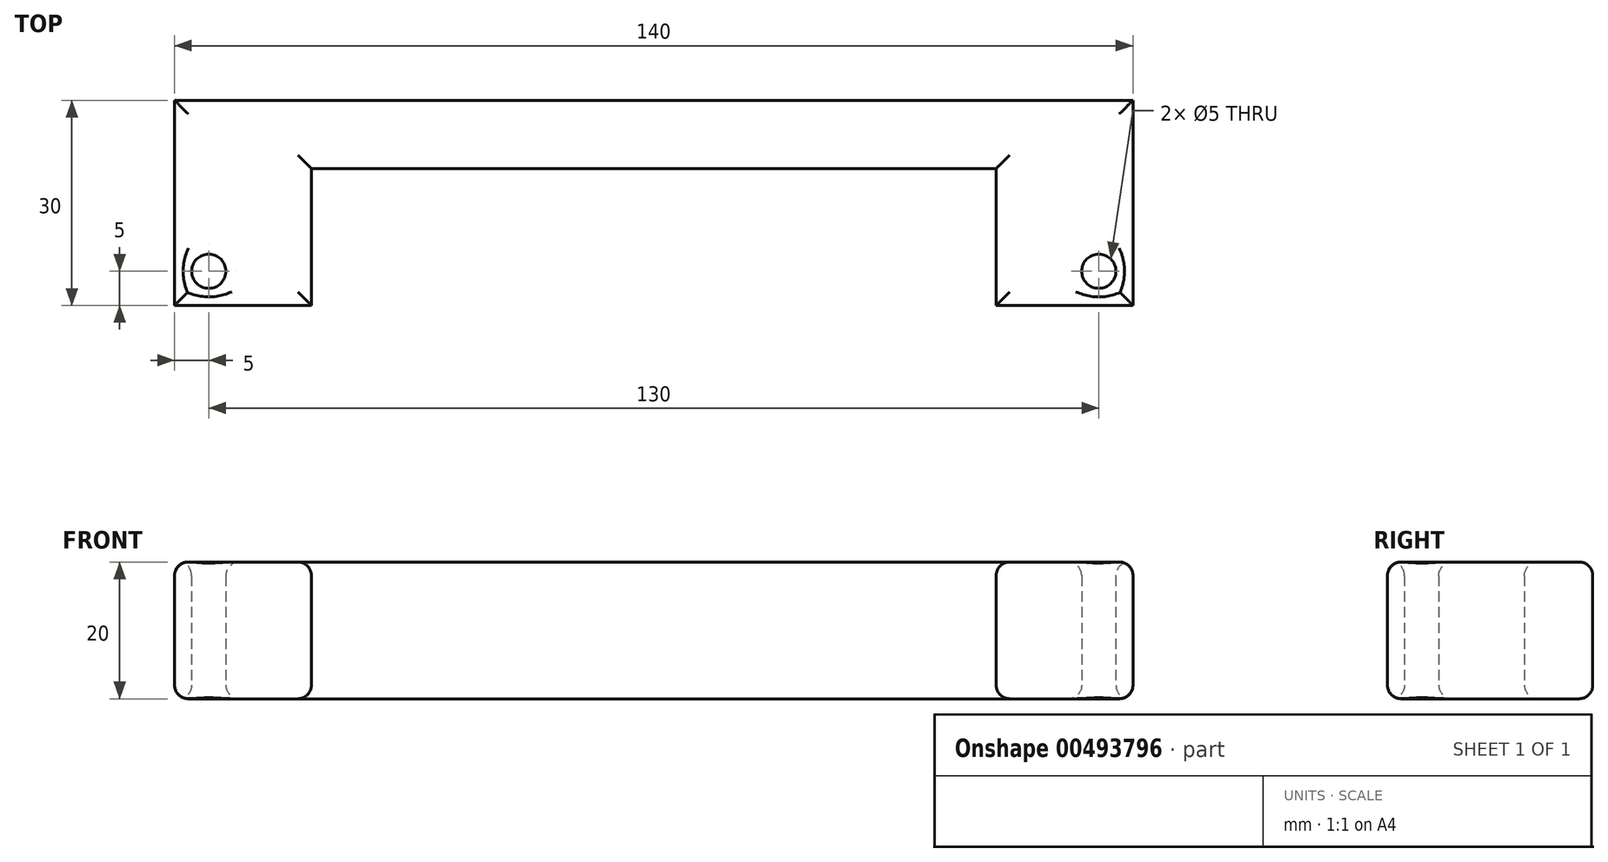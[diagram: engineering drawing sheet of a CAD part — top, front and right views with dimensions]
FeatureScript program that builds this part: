
annotation { "Feature Type Name" : "Feature", "Feature Type Description" : "" }
export const myFeature = defineFeature(function(context is Context, id is Id, definition is map)
    precondition{}
    {
        {
            var Q0;
            Q0=qCreatedBy(makeId("Top.planeOp"),FACE);
            var sketch = newSketch(context, id + "F0", { "sketchPlane" : qUnion([Q0])});
            skLineSegment(sketch, "E0", {"start": v(0, 30) * mm, "end": v(0, 20) * mm});
            skLineSegment(sketch, "E1", {"start": v(0, 20) * mm, "end": v(50, 20) * mm});
            skLineSegment(sketch, "E2", {"start": v(50, 20) * mm, "end": v(50, 0) * mm});
            skLineSegment(sketch, "E3", {"start": v(50, 0) * mm, "end": v(70, 0) * mm});
            skLineSegment(sketch, "E4", {"start": v(70, 0) * mm, "end": v(70, 30) * mm});
            skLineSegment(sketch, "E5", {"start": v(0, 30) * mm, "end": v(70, 30) * mm});
            skLineSegment(sketch, "E6", {"start": v(70, 30) * mm, "end": v(70, 30) * mm});
            skSolve(sketch);
        }
        {
            var Q0;
            Q0 = qSketchRegion(id + "F0", true);
            extrude(context, id + "F1", {"entities" : qUnion([Q0]), "depth" : 20 * mm});
        }
        {
            var Q0;
            Q0=qCreatedBy(makeId("Top.planeOp"),FACE);
            var sketch = newSketch(context, id + "F2", { "sketchPlane" : qUnion([Q0])});
            skPoint(sketch, "E7", {"position": v(65, 5) * mm});
            skSolve(sketch);
        }
        {
            var Q0;
            Q0=sQuery(id+"F2.wireOp",VERTEX,"E7");
            var Q1;
            Q1=makeQuery(id+"F1.opExtrude","SWEPT_BODY",BODY,{"disambiguationData":[OSD([sQuery(id+"F0.wireOp",EDGE,"E0"),sQuery(id+"F0.wireOp",EDGE,"E1"),sQuery(id+"F0.wireOp",EDGE,"E2"),sQuery(id+"F0.wireOp",EDGE,"E3"),sQuery(id+"F0.wireOp",EDGE,"E4"),sQuery(id+"F0.wireOp",EDGE,"E5")])]});
            hole(context, id + "F3", {"style" : HoleStyle.SIMPLE, "endStyle" : HoleEndStyle.THROUGH, "oppositeDirection" : true, "holeDiameter" : 5 * mm, "isTappedThrough" : true, "tappedDepth" : 12 * mm, "tapClearance" : 3, "locations" : qUnion([Q0]), "scope" : qUnion([Q1])});
        }
        {
            var Q0;
            Q0=makeQuery(id+"F1.opExtrude","SWEPT_BODY",BODY,{"disambiguationData":[OSD([sQuery(id+"F0.wireOp",EDGE,"E0"),sQuery(id+"F0.wireOp",EDGE,"E1"),sQuery(id+"F0.wireOp",EDGE,"E2"),sQuery(id+"F0.wireOp",EDGE,"E3"),sQuery(id+"F0.wireOp",EDGE,"E4"),sQuery(id+"F0.wireOp",EDGE,"E5")])]});
            var Q1;
            Q1=makeQuery(id+"F1.opExtrude","SWEPT_FACE",FACE,{"disambiguationData":[OSD([sQuery(id+"F0.wireOp",EDGE,"E0")])]});
            mirror(context, id + "F4", {"operationType" : NewBodyOperationType.ADD, "entities" : qUnion([Q0]), "mirrorPlane" : qUnion([Q1])});
        }
        {
            var Q0;
            {var subQ0=makeQuery(id+"F1.opExtrude","CAP_FACE",FACE,{"disambiguationData":[OSD([sQuery(id+"F0.wireOp",EDGE,"E0"),sQuery(id+"F0.wireOp",EDGE,"E1"),sQuery(id+"F0.wireOp",EDGE,"E2"),sQuery(id+"F0.wireOp",EDGE,"E3"),sQuery(id+"F0.wireOp",EDGE,"E4"),sQuery(id+"F0.wireOp",EDGE,"E5")])],"isStart":false});Q0=makeQuery(id+"F4.boolean.opBoolean","MERGE",FACE,{"derivedFrom":[subQ0,makeQuery(id+"F4.opPattern","COPY",FACE,{"derivedFrom":subQ0,"instanceName":"1"})]});}
            var Q1;
            {var subQ0=makeQuery(id+"F1.opExtrude","CAP_FACE",FACE,{"disambiguationData":[OSD([sQuery(id+"F0.wireOp",EDGE,"E0"),sQuery(id+"F0.wireOp",EDGE,"E1"),sQuery(id+"F0.wireOp",EDGE,"E2"),sQuery(id+"F0.wireOp",EDGE,"E3"),sQuery(id+"F0.wireOp",EDGE,"E4"),sQuery(id+"F0.wireOp",EDGE,"E5")])],"isStart":true});Q1=makeQuery(id+"F4.boolean.opBoolean","MERGE",FACE,{"derivedFrom":[subQ0,makeQuery(id+"F4.opPattern","COPY",FACE,{"derivedFrom":subQ0,"instanceName":"1"})]});}
            fillet(context, id + "F5", {"entities" : qUnion([Q0, Q1]), "radius" : 2 * mm, "tangentPropagation" : true, "allowEdgeOverflow" : false});
        }
    });
